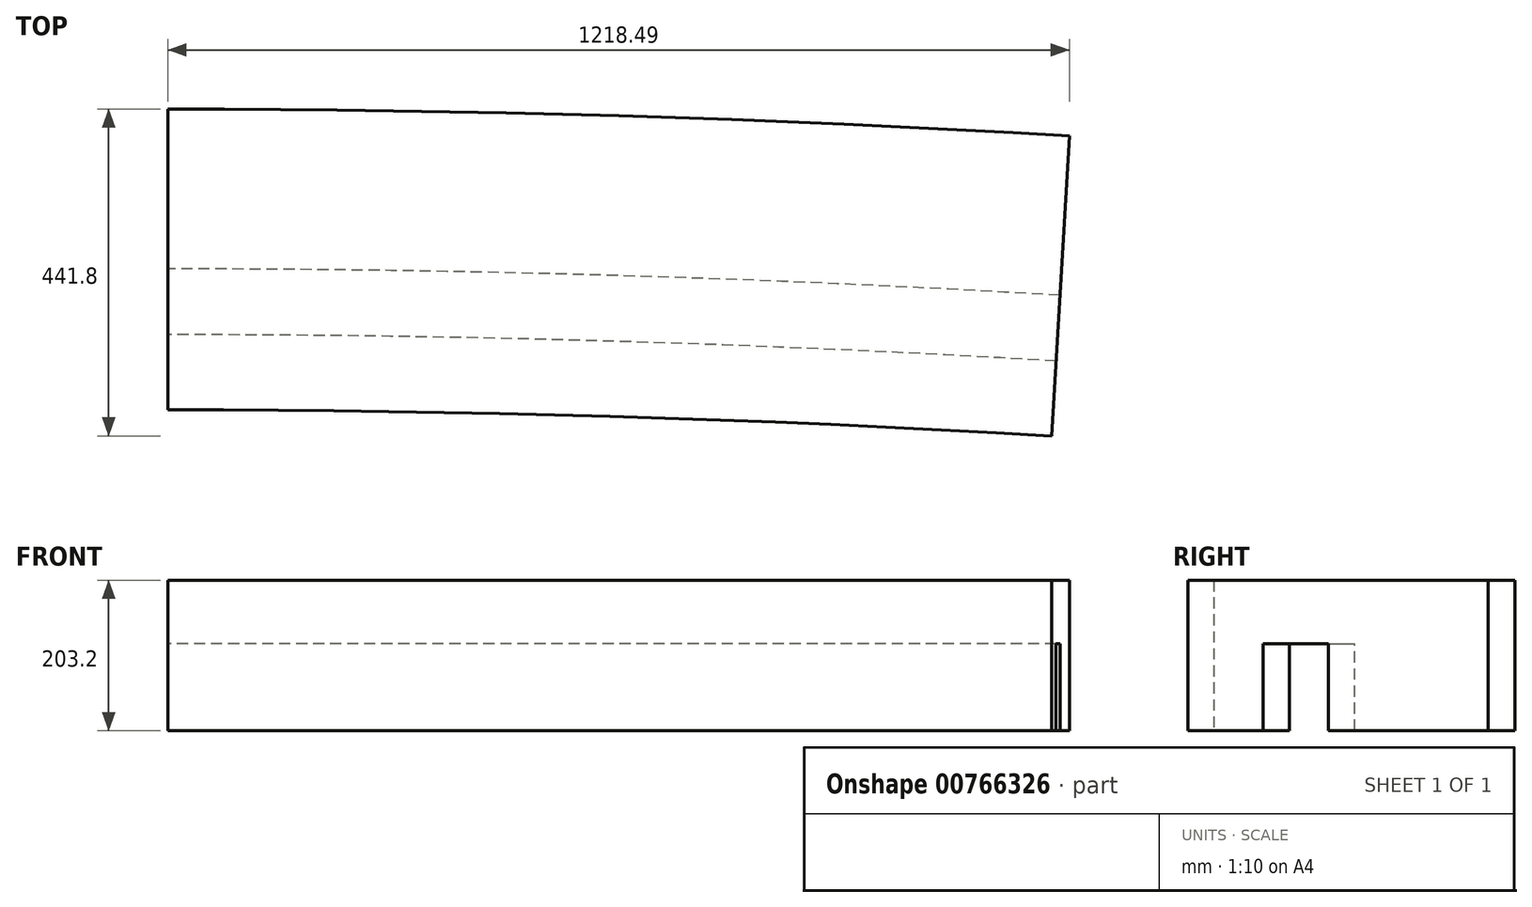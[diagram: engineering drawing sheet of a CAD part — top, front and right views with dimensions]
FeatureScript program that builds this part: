
annotation { "Feature Type Name" : "Feature", "Feature Type Description" : "" }
export const myFeature = defineFeature(function(context is Context, id is Id, definition is map)
    precondition{}
    {
        {
            var Q0;
            Q0=qCreatedBy(makeId("Top.planeOp"),FACE);
            var sketch = newSketch(context, id + "F0", { "sketchPlane" : qUnion([Q0])});
            skArc(sketch, "E0", {"start": v(1218.49, 20537.89) * mm, "mid": v(609.51, 20564.97) * mm, "end": v(0, 20574) * mm});
            skLineSegment(sketch, "E1", {"start": v(0, 20167.6) * mm, "end": v(0, 20574) * mm});
            skLineSegment(sketch, "E2", {"start": v(1194.42, 20132.2) * mm, "end": v(1218.49, 20537.89) * mm});
            skArc(sketch, "E3", {"start": v(1194.42, 20132.2) * mm, "mid": v(597.47, 20158.75) * mm, "end": v(0, 20167.6) * mm});
            skArc(sketch, "E4", {"start": v(1200.43, 20233.62) * mm, "mid": v(600.48, 20260.3) * mm, "end": v(0, 20269.2) * mm, "construction": true});
            skSolve(sketch);
        }
        {
            var Q0;
            Q0 = qSketchRegion(id + "F0", true);
            extrude(context, id + "F1", {"entities" : qUnion([Q0]), "depth" : 203.2 * mm, "offsetDistance" : 25.4 * mm});
        }
        {
            var Q0;
            Q0=makeQuery(id+"F1.opExtrude","SWEPT_FACE",FACE,{"disambiguationData":[OSD([sQuery(id+"F0.wireOp",EDGE,"E2")])]});
            var sketch = newSketch(context, id + "F2", { "sketchPlane" : qUnion([Q0])});
            skLineSegment(sketch, "E5.bottom", {"start": v(20269.2, 0) * mm, "end": v(20358.1, 0) * mm});
            skLineSegment(sketch, "E5.top", {"start": v(20269.2, 117.48) * mm, "end": v(20358.1, 117.48) * mm});
            skLineSegment(sketch, "E5.left", {"start": v(20269.2, 0) * mm, "end": v(20269.2, 117.48) * mm});
            skLineSegment(sketch, "E5.right", {"start": v(20358.1, 0) * mm, "end": v(20358.1, 117.48) * mm});
            skSolve(sketch);
        }
        {
            var Q0;
            Q0=makeQuery(id+"F0.imprint","IMPRINT",FACE,{"disambiguationData":[TD([[makeQuery(id+"F0.imprint","IMPRINT",EDGE,{"derivedFrom":sQuery(id+"F0.wireOp",EDGE,"E0")}),1.0]])]});
            var sketch = newSketch(context, id + "F3", { "sketchPlane" : qUnion([Q0])});
            skArc(sketch, "E6.0", {"start": v(1200.43, 20233.62) * mm, "mid": v(600.48, 20260.3) * mm, "end": v(0, 20269.2) * mm});
            skSolve(sketch);
        }
        {
            var Q0;
            Q0 = qSketchRegion(id + "F2", true);
            var Q1;
            Q1=sQuery(id+"F3.wireOp",EDGE,"E6.0");
            sweep(context, id + "F4", {"operationType" : NewBodyOperationType.REMOVE, "profiles" : qUnion([Q0]), "path" : qUnion([Q1])});
        }
    });
